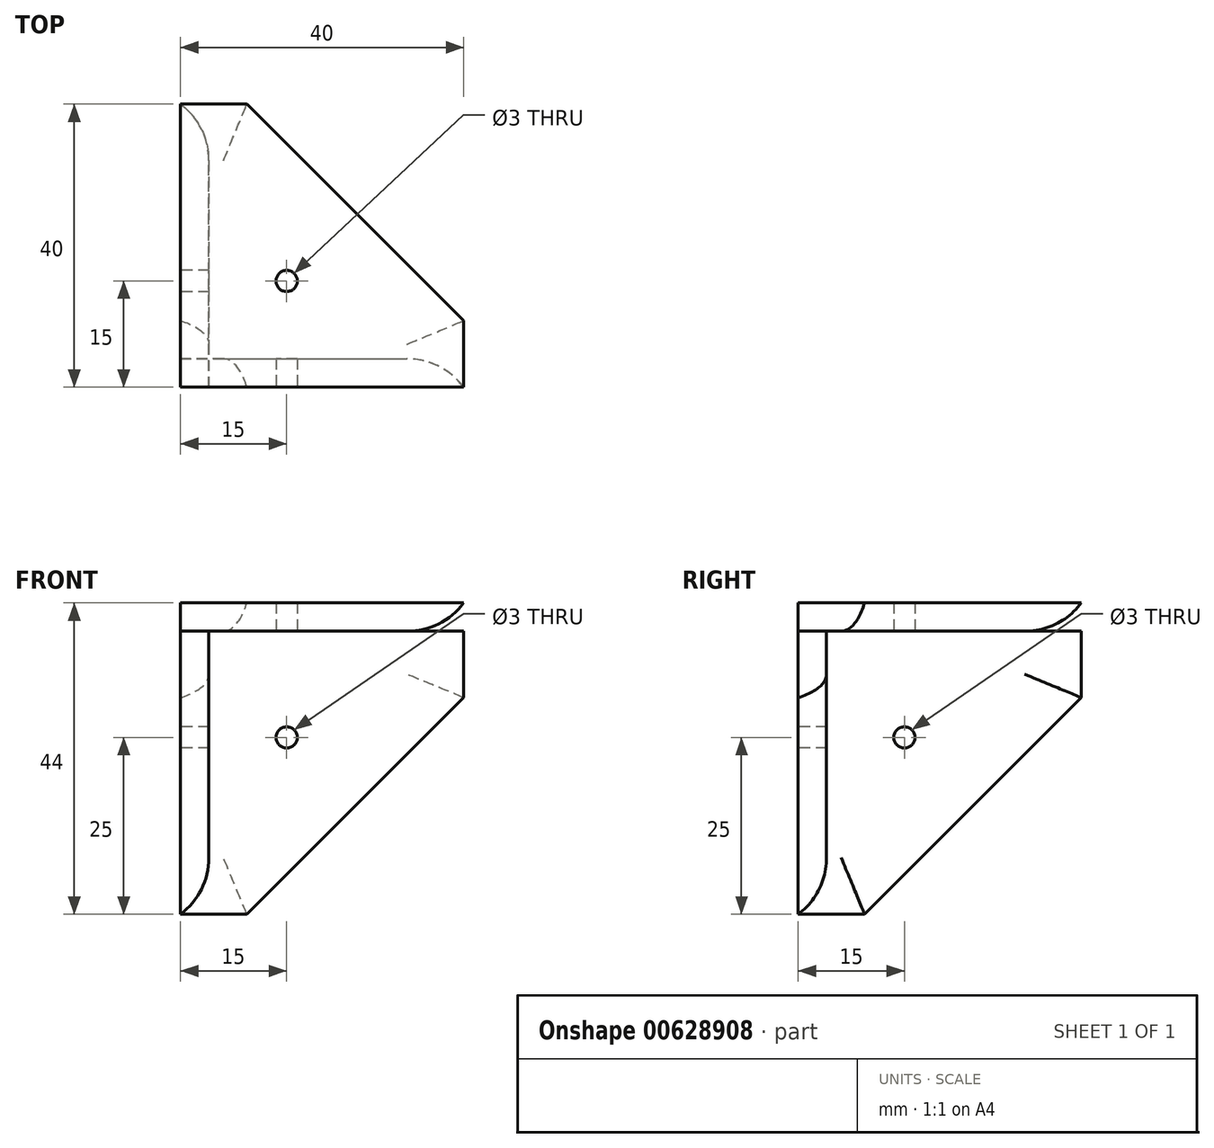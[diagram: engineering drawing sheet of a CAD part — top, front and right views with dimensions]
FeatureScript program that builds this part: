
annotation { "Feature Type Name" : "Feature", "Feature Type Description" : "" }
export const myFeature = defineFeature(function(context is Context, id is Id, definition is map)
    precondition{}
    {
        {
            var Q0;
            Q0=qCreatedBy(makeId("Front.planeOp"),FACE);
            var sketch = newSketch(context, id + "F0", { "sketchPlane" : qUnion([Q0])});
            skLineSegment(sketch, "E0.bottom", {"start": v(0, 0) * mm, "end": v(40, 0) * mm});
            skLineSegment(sketch, "E0.top", {"start": v(0, -40) * mm, "end": v(40, -40) * mm});
            skLineSegment(sketch, "E0.left", {"start": v(0, 0) * mm, "end": v(0, -40) * mm});
            skLineSegment(sketch, "E0.right", {"start": v(40, 0) * mm, "end": v(40, -40) * mm});
            skLineSegment(sketch, "E1", {"start": v(57.97, 8.58) * mm, "end": v(-37.76, -87.15) * mm});
            skPoint(sketch, "E2", {"position": v(0, -15) * mm});
            skPoint(sketch, "E3", {"position": v(15, 0) * mm});
            skCircle(sketch, "E4", {"center": v(15, -15) * mm, "radius": 1.5 * mm});
            skSolve(sketch);
        }
        {
            var Q0;
            {var subQ1=sQuery(id+"F0.wireOp",EDGE,"E0.bottom");Q0=makeQuery(id+"F0.imprint","IMPRINT",FACE,{"disambiguationData":[TD([[makeQuery(id+"F0.imprint","IMPRINT",EDGE,{"derivedFrom":subQ1}),-1.0]])]});}
            extrude(context, id + "F1", {"entities" : qUnion([Q0]), "oppositeDirection" : true, "depth" : 4 * mm, "offsetDistance" : 25 * mm});
        }
        {
            var Q0;
            Q0=makeQuery(id+"F1.opExtrude","SWEPT_BODY",BODY,{"disambiguationData":[OSD([sQuery(id+"F0.wireOp",EDGE,"E0.bottom"),sQuery(id+"F0.wireOp",EDGE,"E0.top"),sQuery(id+"F0.wireOp",EDGE,"E0.left"),sQuery(id+"F0.wireOp",EDGE,"E0.right"),sQuery(id+"F0.wireOp",EDGE,"E1"),sQuery(id+"F0.wireOp",EDGE,"E4")])]});
            var Q1;
            Q1=makeQuery(id+"F1.opExtrude","CAP_EDGE",EDGE,{"disambiguationData":[OSD([sQuery(id+"F0.wireOp",EDGE,"E0.bottom")])],"isStart":true});
            transform(context, id + "F2", {"entities" : qUnion([Q0]), "transformType" : TransformType.ROTATION, "transformAxis" : qUnion([Q1]), "angle" : 90 * degree, "makeCopy" : true});
        }
        {
            var Q0;
            Q0=makeQuery(id+"F2.opPattern","COPY",BODY,{"derivedFrom":makeQuery(id+"F1.opExtrude","SWEPT_BODY",BODY,{"disambiguationData":[OSD([sQuery(id+"F0.wireOp",EDGE,"E0.bottom"),sQuery(id+"F0.wireOp",EDGE,"E0.top"),sQuery(id+"F0.wireOp",EDGE,"E0.left"),sQuery(id+"F0.wireOp",EDGE,"E0.right"),sQuery(id+"F0.wireOp",EDGE,"E1"),sQuery(id+"F0.wireOp",EDGE,"E4")])]}),"instanceName":"1"});
            var Q1;
            Q1=makeQuery(id+"F2.opPattern","COPY",EDGE,{"derivedFrom":makeQuery(id+"F1.opExtrude","CAP_EDGE",EDGE,{"disambiguationData":[OSD([sQuery(id+"F0.wireOp",EDGE,"E0.left")])],"isStart":true}),"instanceName":"1"});
            transform(context, id + "F3", {"entities" : qUnion([Q0]), "transformType" : TransformType.ROTATION, "transformAxis" : qUnion([Q1]), "angle" : 90 * degree, "makeCopy" : true});
        }
        {
            var Q0;
            Q0=makeQuery(id+"F1.opExtrude","CAP_EDGE",EDGE,{"disambiguationData":[OSD([sQuery(id+"F0.wireOp",EDGE,"E1")])],"isStart":false});
            var Q1;
            Q1=makeQuery(id+"F3.opPattern","COPY",EDGE,{"derivedFrom":makeQuery(id+"F2.opPattern","COPY",EDGE,{"derivedFrom":makeQuery(id+"F1.opExtrude","CAP_EDGE",EDGE,{"disambiguationData":[OSD([sQuery(id+"F0.wireOp",EDGE,"E1")])],"isStart":false}),"instanceName":"1"}),"instanceName":"1"});
            var Q2;
            Q2=makeQuery(id+"F2.opPattern","COPY",EDGE,{"derivedFrom":makeQuery(id+"F1.opExtrude","CAP_EDGE",EDGE,{"disambiguationData":[OSD([sQuery(id+"F0.wireOp",EDGE,"E1")])],"isStart":true}),"instanceName":"1"});
            var Q3;
            Q3=makeQuery(id+"F1.opExtrude","CAP_EDGE",EDGE,{"disambiguationData":[OSD([sQuery(id+"F0.wireOp",EDGE,"E0.top")])],"isStart":false});
            var Q4;
            Q4=makeQuery(id+"F3.opPattern","COPY",EDGE,{"derivedFrom":makeQuery(id+"F2.opPattern","COPY",EDGE,{"derivedFrom":makeQuery(id+"F1.opExtrude","CAP_EDGE",EDGE,{"disambiguationData":[OSD([sQuery(id+"F0.wireOp",EDGE,"E0.right")])],"isStart":false}),"instanceName":"1"}),"instanceName":"1"});
            var Q5;
            Q5=makeQuery(id+"F3.opPattern","COPY",EDGE,{"derivedFrom":makeQuery(id+"F2.opPattern","COPY",EDGE,{"derivedFrom":makeQuery(id+"F1.opExtrude","CAP_EDGE",EDGE,{"disambiguationData":[OSD([sQuery(id+"F0.wireOp",EDGE,"E0.top")])],"isStart":false}),"instanceName":"1"}),"instanceName":"1"});
            var Q6;
            Q6=makeQuery(id+"F2.opPattern","COPY",EDGE,{"derivedFrom":makeQuery(id+"F1.opExtrude","CAP_EDGE",EDGE,{"disambiguationData":[OSD([sQuery(id+"F0.wireOp",EDGE,"E0.top")])],"isStart":true}),"instanceName":"1"});
            var Q7;
            Q7=makeQuery(id+"F1.opExtrude","CAP_EDGE",EDGE,{"disambiguationData":[OSD([sQuery(id+"F0.wireOp",EDGE,"E0.right")])],"isStart":false});
            var Q8;
            Q8=makeQuery(id+"F2.opPattern","COPY",EDGE,{"derivedFrom":makeQuery(id+"F1.opExtrude","CAP_EDGE",EDGE,{"disambiguationData":[OSD([sQuery(id+"F0.wireOp",EDGE,"E0.right")])],"isStart":true}),"instanceName":"1"});
            fillet(context, id + "F4", {"entities" : qUnion([Q0, Q1, Q2, Q3, Q4, Q5, Q6, Q7, Q8]), "radius" : 10 * mm, "tangentPropagation" : true, "allowEdgeOverflow" : false});
        }
    });
